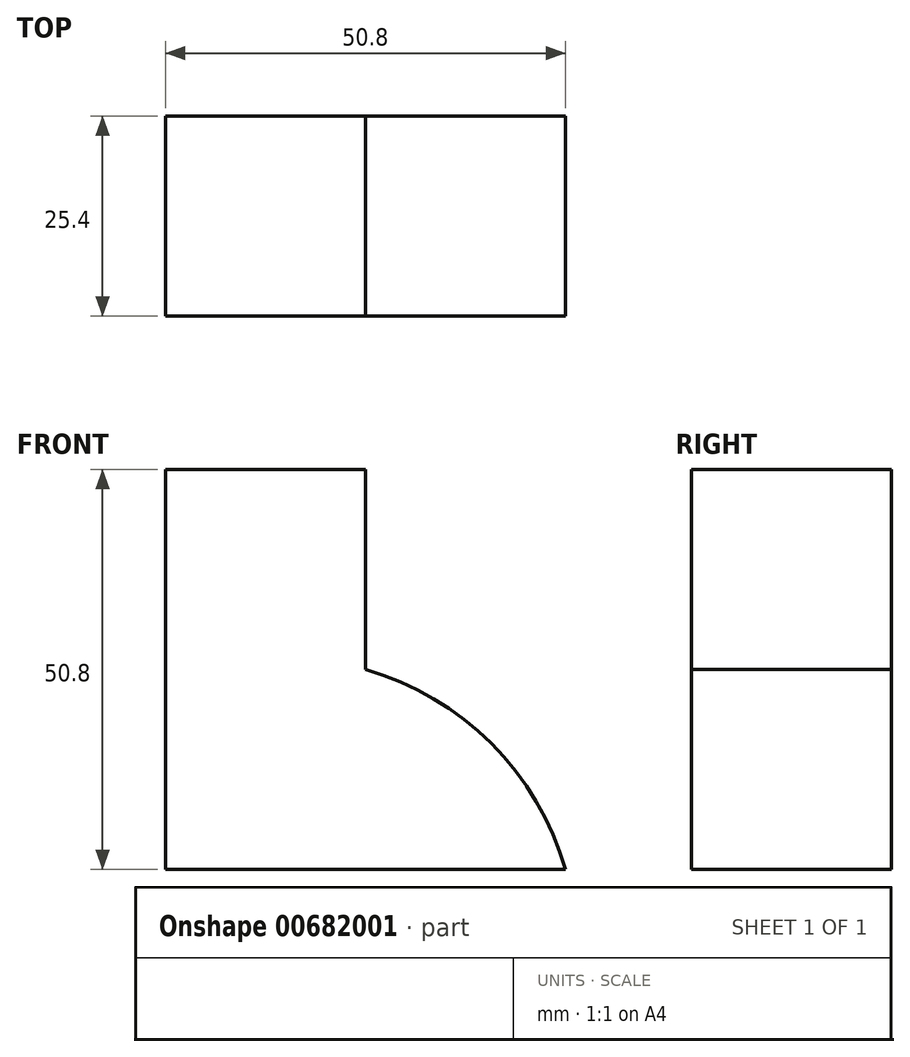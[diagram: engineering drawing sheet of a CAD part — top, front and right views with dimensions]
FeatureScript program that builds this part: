
annotation { "Feature Type Name" : "Feature", "Feature Type Description" : "" }
export const myFeature = defineFeature(function(context is Context, id is Id, definition is map)
    precondition{}
    {
        {
            var Q0;
            Q0=qCreatedBy(makeId("Front.planeOp"),FACE);
            var sketch = newSketch(context, id + "F0", { "sketchPlane" : qUnion([Q0])});
            skLineSegment(sketch, "E0", {"start": v(0, 0) * mm, "end": v(-50.8, 0) * mm});
            skLineSegment(sketch, "E1", {"start": v(-50.8, 0) * mm, "end": v(-50.8, 50.8) * mm});
            skLineSegment(sketch, "E2", {"start": v(-50.8, 50.8) * mm, "end": v(-25.4, 50.8) * mm});
            skLineSegment(sketch, "E3", {"start": v(-25.4, 50.8) * mm, "end": v(-25.4, 25.4) * mm});
            skArc(sketch, "E4", {"start": v(0, 0) * mm, "mid": v(-9.42, 15.98) * mm, "end": v(-25.4, 25.4) * mm});
            skSolve(sketch);
        }
        {
            var Q0;
            Q0=makeQuery(id+"F0.imprint","IMPRINT",FACE,{"disambiguationData":[TD([[makeQuery(id+"F0.imprint","IMPRINT",EDGE,{"derivedFrom":sQuery(id+"F0.wireOp",EDGE,"E0")}),-1.0]])]});
            extrude(context, id + "F1", {"entities" : qUnion([Q0]), "depth" : 25.4 * mm, "offsetDistance" : 25.4 * mm});
        }
    });
